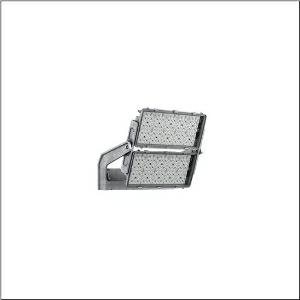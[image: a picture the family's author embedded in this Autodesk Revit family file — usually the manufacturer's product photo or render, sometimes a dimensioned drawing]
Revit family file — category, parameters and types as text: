
# Revit family: floodlight_fl_11_maxi___rs12_5xa779114m01ba_e627
name_source: partatom
category: Lighting Fixtures
units: mm (PartAtom-declared; Revit-internal decimal feet)

## family parameters
Cut with Voids When Loaded = No
Host = Face
Light Source = No
Part Type = Normal
Room Calculation Point = No
Round Connector Dimension = Use Diameter
Shared = No

## types (1)
- --- (1 x LED, 76660 lm, 707.9 W, 5700K)
    Apparent Load = 708 VA
    CIE Flux Codes = 79 92 99 100 100
    Color Rendering = 90
    Color Temperature = 5700K
    Default Elevation = 1800 mm
    Description = Floodlight FL 11  maxi floodlight; light control with lens of PMMA; cover panel of toughened safety glass, transparent; light distribution: RS12, rotationally symmetric direct distribution, LEDcolour temperature: 5700K, rated luminous flux: 76.600lm, colour rendering: CRI > 90, light colour: 957; luminous efficacy: 108lm/W; brightness control: DALI 2 (1 DALI address); with terminal, 5-pole, max. 2.5mm², mains connection: 220..240V/380..400V AC, 50/60Hz, surge voltage resistance: line to ground: 10kV, dustproof LED module, LED unit replaceable without ESD environment, ECG replaceable separately, dimming range 10..100%; 708W floodlight with 2x LED unit of diecast aluminium, coated grey; length: 713mm / width: 651mm / height: 338mm; housing frame, of diecast aluminium, uncoated, natural, mounting bracket, of diecast aluminium, uncoated, natural, equipment: Longlife, protection rating (complete): IP66; insulation class (complete): insulation class I (protective earthing); certification: CE, ENEC, VDE; ball protection: ball impact resistant, only for outdoor installations, rated ambient temperature 10°C, permissible operating ambient temperature: -40..+30°C, permissible storage temperature: -40..+85°C; packaging unit: 1 piece

Light Distribution: RS12
    Height = 320 mm
    Lamp = 1 x LED
    Lamp Light Flux = 76660 lm
    Lamp Power = 707.9 W
    Lamp count = 1
    Length = 712 mm
    Luminous efficacy = 108 lm/W
    Manufacturer = Siteco
    ModVariant = No
    Model = 5XA779114M01BA
    Number of Poles = 1
    OnlyDefault = Yes
    Power Factor = 1
    Product Name = Floodlight FL 11 maxi | RS12
    Product group = floodlight | pylon top
    ProductGroupID = 6101
    Protection Class = Protection class I
    Protection Degree = IP 66
    RLX_Detail_Level = 1
    RlxData = <blob elided: 41829 chars, md5=b61a686e>
    Socket = socket
    Standby Power = 0 W
    System Light Flux = 76660 lm
    System Power = 708 W
    Type Comments = factory setting: luminous flux: 100 % | dim-lin: 254 | 740 mA
    Type Image = l_1006932.jpg
    URL = http://relux.com
    VarID = @adj_095733
    Voltage = 0 V
    Weight = 0.00 kg
    Width = 655 mm

## geometry (parser evidence)
native form markers: Blend x4, Sweep x14
no freeform markers — native parametric forms only
